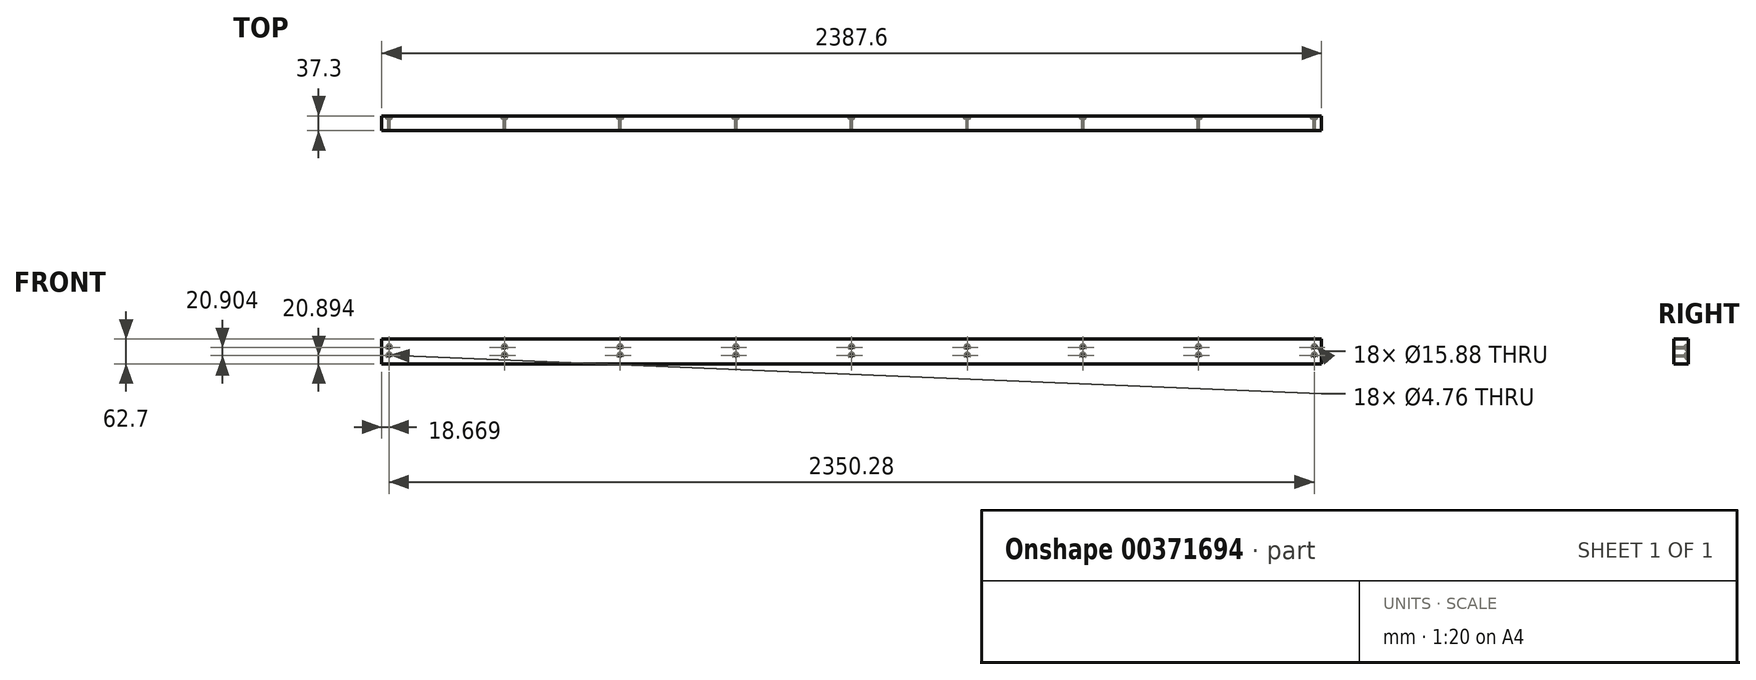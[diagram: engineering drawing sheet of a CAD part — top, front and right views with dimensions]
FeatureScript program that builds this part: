
annotation { "Feature Type Name" : "Feature", "Feature Type Description" : "" }
export const myFeature = defineFeature(function(context is Context, id is Id, definition is map)
    precondition{}
    {
        {
            var Q0;
            Q0=qCreatedBy(makeId("Front.planeOp"),FACE);
            var sketch = newSketch(context, id + "F0", { "sketchPlane" : qUnion([Q0])});
            skLineSegment(sketch, "E0.bottom", {"start": v(-1193.8, 31.35) * mm, "end": v(1193.8, 31.35) * mm});
            skLineSegment(sketch, "E0.top", {"start": v(-1193.8, -31.35) * mm, "end": v(1193.8, -31.35) * mm});
            skLineSegment(sketch, "E0.left", {"start": v(-1193.8, 31.35) * mm, "end": v(-1193.8, -31.35) * mm});
            skLineSegment(sketch, "E0.right", {"start": v(1193.8, 31.35) * mm, "end": v(1193.8, -31.35) * mm});
            skPoint(sketch, "E0.middle", {"position": v(0, 0) * mm});
            skSolve(sketch);
        }
        {
            var Q0;
            Q0=makeQuery(id+"F0.imprint","IMPRINT",FACE,{"disambiguationData":[TD([[makeQuery(id+"F0.imprint","IMPRINT",EDGE,{"derivedFrom":sQuery(id+"F0.wireOp",EDGE,"E0.bottom")}),-1.0]])]});
            extrude(context, id + "F1", {"entities" : qUnion([Q0]), "depth" : 37.3 * mm});
        }
        {
            var Q0;
            Q0=makeQuery(id+"F1.opExtrude","CAP_FACE",FACE,{"disambiguationData":[OSD([sQuery(id+"F0.wireOp",EDGE,"E0.bottom"),sQuery(id+"F0.wireOp",EDGE,"E0.top"),sQuery(id+"F0.wireOp",EDGE,"E0.left"),sQuery(id+"F0.wireOp",EDGE,"E0.right")])],"isStart":true});
            var sketch = newSketch(context, id + "F2", { "sketchPlane" : qUnion([Q0])});
            skPoint(sketch, "E1", {"position": v(-1175.14, 10.45) * mm});
            skPoint(sketch, "E2", {"position": v(-1175.14, -10.46) * mm});
            skPoint(sketch, "E3", {"position": v(-881.27, 10.45) * mm});
            skPoint(sketch, "E4", {"position": v(-881.27, -10.46) * mm});
            skPoint(sketch, "E5", {"position": v(-587.39, 10.45) * mm});
            skPoint(sketch, "E6", {"position": v(-587.39, -10.46) * mm});
            skPoint(sketch, "E7", {"position": v(-293.5, 10.45) * mm});
            skPoint(sketch, "E8", {"position": v(-293.5, -10.46) * mm});
            skPoint(sketch, "E9", {"position": v(0.37, 10.45) * mm});
            skPoint(sketch, "E10", {"position": v(0.37, -10.46) * mm});
            skPoint(sketch, "E11", {"position": v(294.25, 10.45) * mm});
            skPoint(sketch, "E12", {"position": v(294.25, -10.46) * mm});
            skPoint(sketch, "E13", {"position": v(588.12, 10.45) * mm});
            skPoint(sketch, "E14", {"position": v(588.12, -10.46) * mm});
            skPoint(sketch, "E15", {"position": v(882, 10.45) * mm});
            skPoint(sketch, "E16", {"position": v(882, -10.46) * mm});
            skPoint(sketch, "E17", {"position": v(1175.13, 10.45) * mm});
            skPoint(sketch, "E18", {"position": v(1175.13, -10.46) * mm});
            skSolve(sketch);
        }
        {
            var Q0;
            Q0=sQuery(id+"F2.wireOp",VERTEX,"E1");
            var Q1;
            Q1=sQuery(id+"F2.wireOp",VERTEX,"E2");
            var Q2;
            Q2=sQuery(id+"F2.wireOp",VERTEX,"E3");
            var Q3;
            Q3=sQuery(id+"F2.wireOp",VERTEX,"E4");
            var Q4;
            Q4=sQuery(id+"F2.wireOp",VERTEX,"E5");
            var Q5;
            Q5=sQuery(id+"F2.wireOp",VERTEX,"E6");
            var Q6;
            Q6=sQuery(id+"F2.wireOp",VERTEX,"E7");
            var Q7;
            Q7=sQuery(id+"F2.wireOp",VERTEX,"E8");
            var Q8;
            Q8=sQuery(id+"F2.wireOp",VERTEX,"E9");
            var Q9;
            Q9=sQuery(id+"F2.wireOp",VERTEX,"E10");
            var Q10;
            Q10=sQuery(id+"F2.wireOp",VERTEX,"E11");
            var Q11;
            Q11=sQuery(id+"F2.wireOp",VERTEX,"E12");
            var Q12;
            Q12=sQuery(id+"F2.wireOp",VERTEX,"E13");
            var Q13;
            Q13=sQuery(id+"F2.wireOp",VERTEX,"E14");
            var Q14;
            Q14=sQuery(id+"F2.wireOp",VERTEX,"E15");
            var Q15;
            Q15=sQuery(id+"F2.wireOp",VERTEX,"E16");
            var Q16;
            Q16=sQuery(id+"F2.wireOp",VERTEX,"E17");
            var Q17;
            Q17=sQuery(id+"F2.wireOp",VERTEX,"E18");
            var Q18;
            Q18=makeQuery(id+"F1.opExtrude","SWEPT_BODY",BODY,{"disambiguationData":[OSD([sQuery(id+"F0.wireOp",EDGE,"E0.bottom"),sQuery(id+"F0.wireOp",EDGE,"E0.top"),sQuery(id+"F0.wireOp",EDGE,"E0.left"),sQuery(id+"F0.wireOp",EDGE,"E0.right")])]});
            hole(context, id + "F3", {"style" : HoleStyle.SIMPLE, "endStyle" : HoleEndStyle.BLIND, "holeDiameter" : 15.88 * mm, "holeDepth" : 6.35 * mm, "isTappedThrough" : true, "tappedDepth" : 12.7 * mm, "tapClearance" : 3, "locations" : qUnion([Q0, Q1, Q2, Q3, Q4, Q5, Q6, Q7, Q8, Q9, Q10, Q11, Q12, Q13, Q14, Q15, Q16, Q17]), "scope" : qUnion([Q18])});
        }
        {
            var Q0;
            Q0=sQuery(id+"F2.wireOp",VERTEX,"E1");
            var Q1;
            Q1=sQuery(id+"F2.wireOp",VERTEX,"E2");
            var Q2;
            Q2=sQuery(id+"F2.wireOp",VERTEX,"E3");
            var Q3;
            Q3=sQuery(id+"F2.wireOp",VERTEX,"E4");
            var Q4;
            Q4=sQuery(id+"F2.wireOp",VERTEX,"E5");
            var Q5;
            Q5=sQuery(id+"F2.wireOp",VERTEX,"E6");
            var Q6;
            Q6=sQuery(id+"F2.wireOp",VERTEX,"E7");
            var Q7;
            Q7=sQuery(id+"F2.wireOp",VERTEX,"E8");
            var Q8;
            Q8=sQuery(id+"F2.wireOp",VERTEX,"E9");
            var Q9;
            Q9=sQuery(id+"F2.wireOp",VERTEX,"E10");
            var Q10;
            Q10=sQuery(id+"F2.wireOp",VERTEX,"E11");
            var Q11;
            Q11=sQuery(id+"F2.wireOp",VERTEX,"E12");
            var Q12;
            Q12=sQuery(id+"F2.wireOp",VERTEX,"E13");
            var Q13;
            Q13=sQuery(id+"F2.wireOp",VERTEX,"E14");
            var Q14;
            Q14=sQuery(id+"F2.wireOp",VERTEX,"E15");
            var Q15;
            Q15=sQuery(id+"F2.wireOp",VERTEX,"E16");
            var Q16;
            Q16=sQuery(id+"F2.wireOp",VERTEX,"E17");
            var Q17;
            Q17=sQuery(id+"F2.wireOp",VERTEX,"E18");
            var Q18;
            Q18=makeQuery(id+"F1.opExtrude","SWEPT_BODY",BODY,{"disambiguationData":[OSD([sQuery(id+"F0.wireOp",EDGE,"E0.bottom"),sQuery(id+"F0.wireOp",EDGE,"E0.top"),sQuery(id+"F0.wireOp",EDGE,"E0.left"),sQuery(id+"F0.wireOp",EDGE,"E0.right")])]});
            hole(context, id + "F4", {"style" : HoleStyle.SIMPLE, "endStyle" : HoleEndStyle.THROUGH, "holeDiameter" : 4.76 * mm, "isTappedThrough" : true, "tappedDepth" : 12.7 * mm, "tapClearance" : 3, "locations" : qUnion([Q0, Q1, Q2, Q3, Q4, Q5, Q6, Q7, Q8, Q9, Q10, Q11, Q12, Q13, Q14, Q15, Q16, Q17]), "scope" : qUnion([Q18])});
        }
    });
